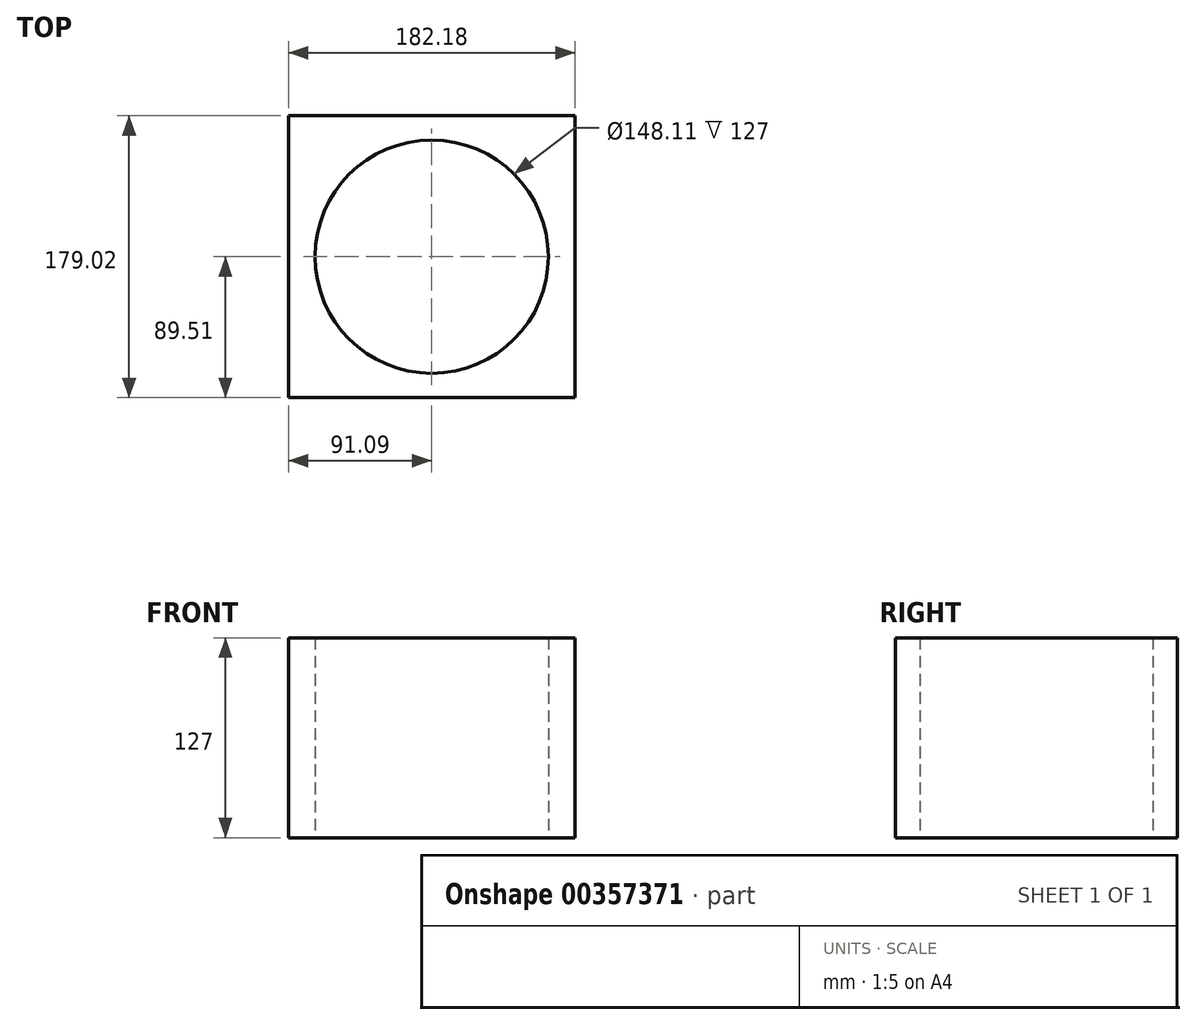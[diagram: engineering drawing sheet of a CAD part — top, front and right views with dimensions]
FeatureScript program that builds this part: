
annotation { "Feature Type Name" : "Feature", "Feature Type Description" : "" }
export const myFeature = defineFeature(function(context is Context, id is Id, definition is map)
    precondition{}
    {
        {
            var Q0;
            Q0=qCreatedBy(makeId("Top.planeOp"),FACE);
            var sketch = newSketch(context, id + "F0", { "sketchPlane" : qUnion([Q0])});
            skLineSegment(sketch, "E0.bottom", {"start": v(-91.1, -89.51) * mm, "end": v(91.1, -89.51) * mm});
            skLineSegment(sketch, "E0.top", {"start": v(-91.1, 89.51) * mm, "end": v(91.1, 89.51) * mm});
            skLineSegment(sketch, "E0.left", {"start": v(-91.1, -89.51) * mm, "end": v(-91.1, 89.51) * mm});
            skLineSegment(sketch, "E0.right", {"start": v(91.1, -89.51) * mm, "end": v(91.1, 89.51) * mm});
            skPoint(sketch, "E0.middle", {"position": v(0, 0) * mm});
            skSolve(sketch);
        }
        {
            var Q0;
            Q0=makeQuery(id+"F0.imprint","IMPRINT",FACE,{"disambiguationData":[TD([[makeQuery(id+"F0.imprint","IMPRINT",EDGE,{"derivedFrom":sQuery(id+"F0.wireOp",EDGE,"E0.bottom")}),1.0]])]});
            var sketch = newSketch(context, id + "F1", { "sketchPlane" : qUnion([Q0])});
            skCircle(sketch, "E1", {"center": v(0, 0) * mm, "radius": 74.06 * mm});
            skSolve(sketch);
        }
        {
            var Q0;
            Q0=makeQuery(id+"F1.imprint","IMPRINT",FACE,{"disambiguationData":[TD([[makeQuery(id+"F1.imprint","IMPRINT",EDGE,{"derivedFrom":sQuery(id+"F1.wireOp",EDGE,"E1")}),-1.0]])]});
            var sketch = newSketch(context, id + "F2", { "sketchPlane" : qUnion([Q0])});
            skSolve(sketch);
        }
        {
            var Q0;
            Q0=makeQuery(id+"F2.imprint","IMPRINT",FACE,{"disambiguationData":[TD([[makeQuery(id+"F2.imprint","IMPRINT",EDGE,{"derivedFrom":makeQuery(id+"F1.imprint","IMPRINT",EDGE,{"derivedFrom":sQuery(id+"F1.wireOp",EDGE,"E1")})}),-1.0]])]});
            extrude(context, id + "F3", {"entities" : qUnion([Q0]), "depth" : 127 * mm});
        }
    });
